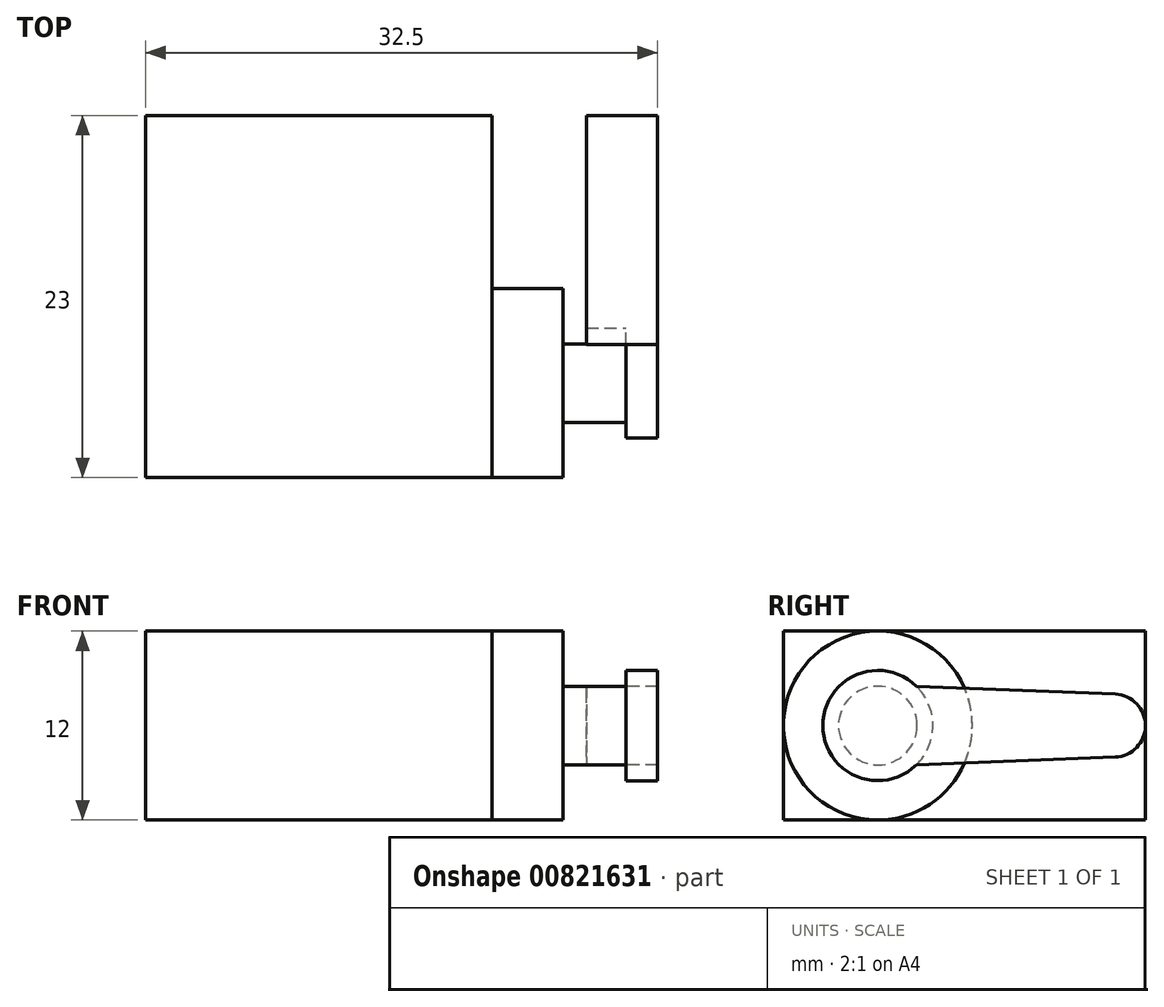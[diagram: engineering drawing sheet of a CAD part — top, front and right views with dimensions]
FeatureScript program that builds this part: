
annotation { "Feature Type Name" : "Feature", "Feature Type Description" : "" }
export const myFeature = defineFeature(function(context is Context, id is Id, definition is map)
    precondition{}
    {
        {
            var Q0;
            Q0=qCreatedBy(makeId("Right.planeOp"),FACE);
            var sketch = newSketch(context, id + "F0", { "sketchPlane" : qUnion([Q0])});
            skLineSegment(sketch, "E0.bottom", {"start": v(-11.5, 6) * mm, "end": v(11.5, 6) * mm});
            skLineSegment(sketch, "E0.top", {"start": v(-11.5, -6) * mm, "end": v(11.5, -6) * mm});
            skLineSegment(sketch, "E0.left", {"start": v(-11.5, 6) * mm, "end": v(-11.5, -6) * mm});
            skLineSegment(sketch, "E0.right", {"start": v(11.5, 6) * mm, "end": v(11.5, -6) * mm});
            skSolve(sketch);
        }
        {
            var Q0;
            Q0=makeQuery(id+"F0.imprint","IMPRINT",FACE,{"disambiguationData":[TD([[makeQuery(id+"F0.imprint","IMPRINT",EDGE,{"derivedFrom":sQuery(id+"F0.wireOp",EDGE,"E0.bottom")}),-1.0]])]});
            extrude(context, id + "F1", {"entities" : qUnion([Q0]), "depth" : 22 * mm, "offsetDistance" : 25 * mm});
        }
        {
            var Q0;
            Q0=makeQuery(id+"F1.opExtrude","CAP_FACE",FACE,{"disambiguationData":[OSD([sQuery(id+"F0.wireOp",EDGE,"E0.bottom"),sQuery(id+"F0.wireOp",EDGE,"E0.top"),sQuery(id+"F0.wireOp",EDGE,"E0.left"),sQuery(id+"F0.wireOp",EDGE,"E0.right")])],"isStart":false});
            var sketch = newSketch(context, id + "F2", { "sketchPlane" : qUnion([Q0])});
            skCircle(sketch, "E1", {"center": v(-5.5, 0) * mm, "radius": 6 * mm});
            skLineSegment(sketch, "E2", {"start": v(-11.5, 0) * mm, "end": v(11.5, 0) * mm, "construction": true});
            skSolve(sketch);
        }
        {
            var Q0;
            {var subQ0=sQuery(id+"F2.wireOp",EDGE,"E1");var subQ1=makeQuery(id+"F2.imprint","INTERSECT",VERTEX,{"derivedFrom":[makeQuery(id+"F1.opExtrude","CAP_EDGE",EDGE,{"disambiguationData":[OSD([sQuery(id+"F0.wireOp",EDGE,"E0.left")])],"isStart":false}),subQ0]});Q0=makeQuery(id+"F2.imprint","IMPRINT",FACE,{"disambiguationData":[TD([[makeQuery(id+"F2.imprint","IMPRINT",EDGE,{"disambiguationData":[TD([[subQ1,1.0]])],"derivedFrom":subQ0}),1.0]])]});}
            extrude(context, id + "F3", {"entities" : qUnion([Q0]), "operationType" : NewBodyOperationType.ADD, "depth" : 4.5 * mm, "offsetDistance" : 25 * mm});
        }
        {
            var Q0;
            Q0=makeQuery(id+"F3.opExtrude","CAP_FACE",FACE,{"disambiguationData":[OSD([sQuery(id+"F2.wireOp",EDGE,"E1")])],"isStart":false});
            var sketch = newSketch(context, id + "F4", { "sketchPlane" : qUnion([Q0])});
            skCircle(sketch, "E3", {"center": v(-5.5, 0) * mm, "radius": 2.5 * mm});
            skSolve(sketch);
        }
        {
            var Q0;
            Q0=makeQuery(id+"F4.imprint","IMPRINT",FACE,{"disambiguationData":[TD([[makeQuery(id+"F4.imprint","IMPRINT",EDGE,{"derivedFrom":sQuery(id+"F4.wireOp",EDGE,"E3")}),1.0]])]});
            extrude(context, id + "F5", {"entities" : qUnion([Q0]), "operationType" : NewBodyOperationType.ADD, "depth" : 4 * mm, "offsetDistance" : 25 * mm});
        }
        {
            var Q0;
            Q0=makeQuery(id+"F5.opExtrude","CAP_FACE",FACE,{"disambiguationData":[OSD([sQuery(id+"F4.wireOp",EDGE,"E3")])],"isStart":false});
            var sketch = newSketch(context, id + "F6", { "sketchPlane" : qUnion([Q0])});
            skLineSegment(sketch, "E4", {"start": v(-5.5, 0) * mm, "end": v(9.5, 0) * mm, "construction": true});
            skArc(sketch, "E5", {"start": v(9.58, -2) * mm, "mid": v(11.5, 0) * mm, "end": v(9.58, 2) * mm});
            skArc(sketch, "E6", {"start": v(-3.05, 2.5) * mm, "mid": v(-9, 0) * mm, "end": v(-3.05, -2.5) * mm});
            skLineSegment(sketch, "E7", {"start": v(9.58, 2) * mm, "end": v(-3.05, 2.5) * mm});
            skLineSegment(sketch, "E8.MirrorCS", {"start": v(9.58, -2) * mm, "end": v(-3.05, -2.5) * mm});
            skSolve(sketch);
        }
        {
            var Q0;
            Q0=makeQuery(id+"F6.imprint","IMPRINT",FACE,{"disambiguationData":[TD([[makeQuery(id+"F6.imprint","IMPRINT",EDGE,{"derivedFrom":sQuery(id+"F6.wireOp",EDGE,"E5")}),1.0]])]});
            var Q1;
            Q1=makeQuery(id+"F6.imprint","IMPRINT",FACE,{"disambiguationData":[TD([[makeQuery(id+"F6.imprint","IMPRINT",EDGE,{"derivedFrom":makeQuery(id+"F5.opExtrude","CAP_EDGE",EDGE,{"disambiguationData":[OSD([sQuery(id+"F4.wireOp",EDGE,"E3")])],"isStart":false})}),1.0]])]});
            extrude(context, id + "F7", {"entities" : qUnion([Q0, Q1]), "operationType" : NewBodyOperationType.ADD, "depth" : 2 * mm, "offsetDistance" : 25 * mm});
        }
        {
            var Q0;
            Q0=makeQuery(id+"F7.opExtrude","CAP_FACE",FACE,{"disambiguationData":[OSD([sQuery(id+"F6.wireOp",EDGE,"E5"),sQuery(id+"F6.wireOp",EDGE,"E6"),sQuery(id+"F6.wireOp",EDGE,"E7"),sQuery(id+"F6.wireOp",EDGE,"E8.MirrorCS")])],"isStart":true});
            var sketch = newSketch(context, id + "F8", { "sketchPlane" : qUnion([Q0])});
            skCircle(sketch, "E9", {"center": v(5.5, 0) * mm, "radius": 3.5 * mm});
            skSolve(sketch);
        }
        {
            var Q0;
            {var subQ0=sQuery(id+"F8.wireOp",EDGE,"E9");Q0=makeQuery(id+"F8.imprint","IMPRINT",FACE,{"disambiguationData":[TD([[makeQuery(id+"F8.imprint","IMPRINT",EDGE,{"disambiguationData":[OD(0.0)],"derivedFrom":subQ0}),-1.0]])]});}
            extrude(context, id + "F9", {"entities" : qUnion([Q0]), "operationType" : NewBodyOperationType.ADD, "depth" : 2.5 * mm, "offsetDistance" : 25 * mm});
        }
    });
